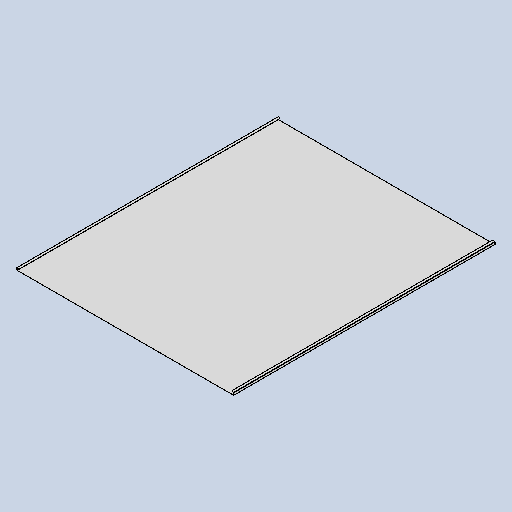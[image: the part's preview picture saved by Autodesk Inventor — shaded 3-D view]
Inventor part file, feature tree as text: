
AUTODESK INVENTOR PART (.ipt)
format: ipt  version: 2025 (Build 290162010, 162A)  size: 201,728 bytes
history: native  units: mm
features: sheet_metal_op x13, other x6, sketch x5, chamfer x4
ambient origin geometry x8: Origin, YZ Plane, XZ Plane, XY Plane, X Axis, Y Axis, Z Axis, Center Point
bodies: Body1 (feature_tree)
feature tree (28):
  sheet_metal_op  "Face1"
  sheet_metal_op  "Flange2"
  sheet_metal_op  "Flange3"
  sheet_metal_op  "Flange4"
  sheet_metal_op  "Flange5"
  chamfer  "Corner Round1"
  chamfer  "Corner Round2"
  chamfer  "Corner Round3"
  chamfer  "Corner Round4"
  sketch  "Sketch6"  dims[d12=23.212879mm]
  other  "Plate2"
  sketch  "Sketch11"  dims[d52=814.2mm]
  other  "Plate4"
  sheet_metal_op  "Bend3"
  sheet_metal_op  "Corner3"
  sketch  "Sketch12"  dims[d53=980.0mm]
  other  "Plate5"
  sheet_metal_op  "Bend4"
  sheet_metal_op  "Corner4"
  sketch  "Sketch13"  dims[d54=0.5mm]
  other  "Plate6"
  sheet_metal_op  "Bend5"
  sheet_metal_op  "Corner5"
  sketch  "Sketch14"  dims[d84=0.5mm d85=0.25mm d86=1.0mm d87=0.5mm d88=10.0mm d89=90.0deg d90=0.5mm d91=2.0mm d92=0.5mm d93=0.5mm d94=0.5mm d95=0.25mm d96=1.0mm d97=0.5mm d98=10.0mm d99=90.0deg d100=0.5mm d101=2.0mm d102=0.5mm d103=0.5mm d104=0.5mm d105=0.25mm d106=1.0mm d107=0.5mm d108=10.0mm d109=90.0deg d110=0.5mm d111=2.0mm d112=0.5mm d113=0.5mm d114=0.5mm d115=0.25mm d116=1.0mm d117=0.5mm d118=10.0mm d119=90.0deg d120=0.5mm d121=2.0mm d122=0.5mm d123=0.5mm d124=4.0mm d125=4.0mm d126=4.0mm d127=4.0mm]
  other  "Plate7"
  sheet_metal_op  "Bend6"
  sheet_metal_op  "Corner6"
  other  "Definition1"
